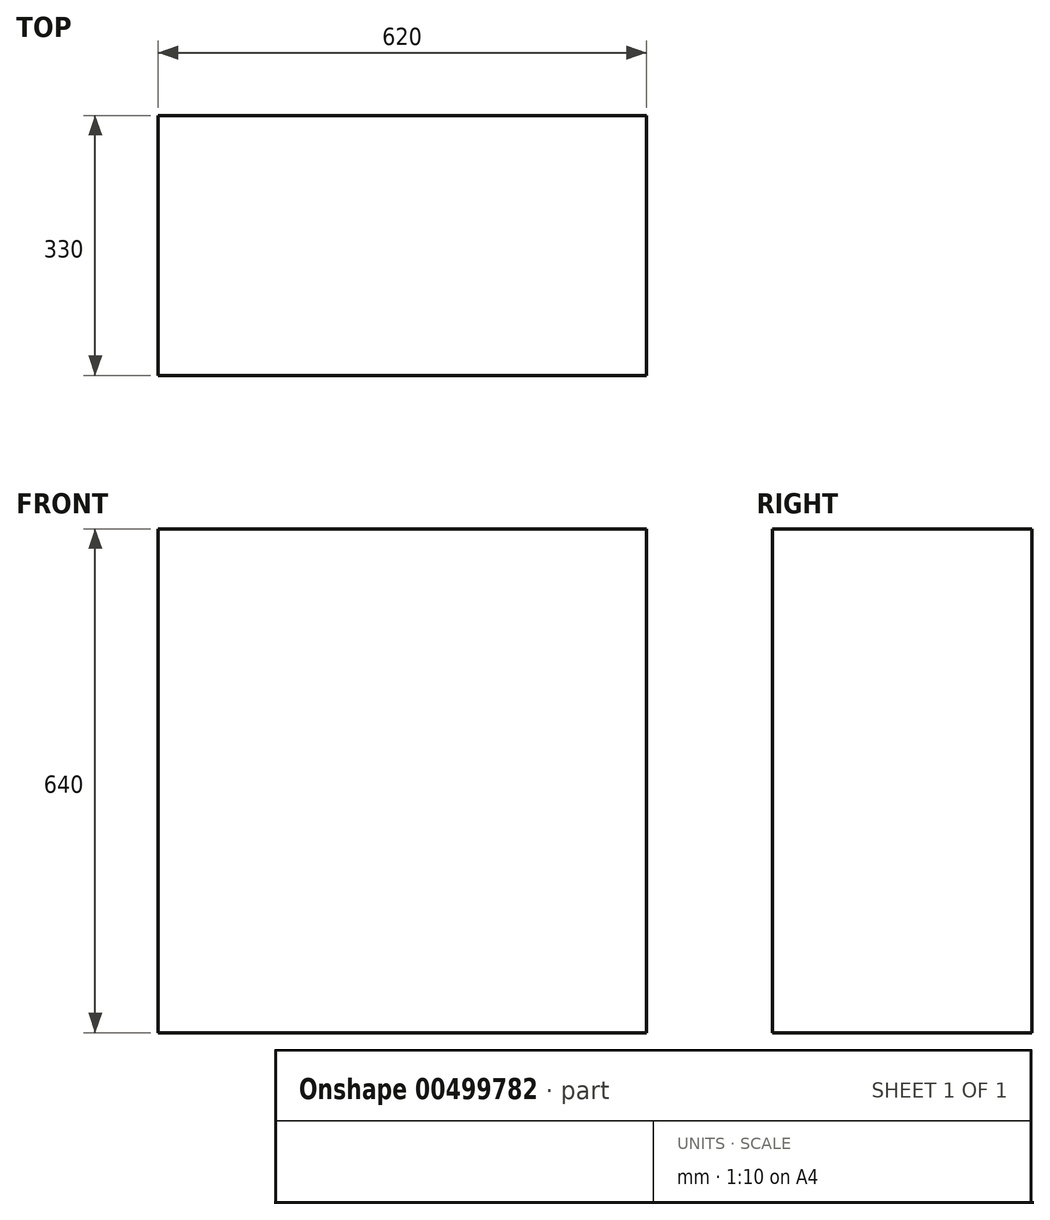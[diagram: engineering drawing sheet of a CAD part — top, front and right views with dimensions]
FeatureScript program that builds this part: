
annotation { "Feature Type Name" : "Feature", "Feature Type Description" : "" }
export const myFeature = defineFeature(function(context is Context, id is Id, definition is map)
    precondition{}
    {
        {
            var Q0;
            Q0=qCreatedBy(makeId("Front.planeOp"),FACE);
            var sketch = newSketch(context, id + "F0", { "sketchPlane" : qUnion([Q0])});
            skLineSegment(sketch, "E0.bottom", {"start": v(-317.37, 318.56) * mm, "end": v(302.63, 318.56) * mm});
            skLineSegment(sketch, "E0.top", {"start": v(-317.37, -321.44) * mm, "end": v(302.63, -321.44) * mm});
            skLineSegment(sketch, "E0.left", {"start": v(-317.37, 318.56) * mm, "end": v(-317.37, -321.44) * mm});
            skLineSegment(sketch, "E0.right", {"start": v(302.63, 318.56) * mm, "end": v(302.63, -321.44) * mm});
            skSolve(sketch);
        }
        {
            var Q0;
            Q0=makeQuery(id+"F0.imprint","IMPRINT",FACE,{"disambiguationData":[TD([[makeQuery(id+"F0.imprint","IMPRINT",EDGE,{"derivedFrom":sQuery(id+"F0.wireOp",EDGE,"E0.bottom")}),-1.0]])]});
            extrude(context, id + "F1", {"entities" : qUnion([Q0]), "depth" : 330 * mm});
        }
    });
